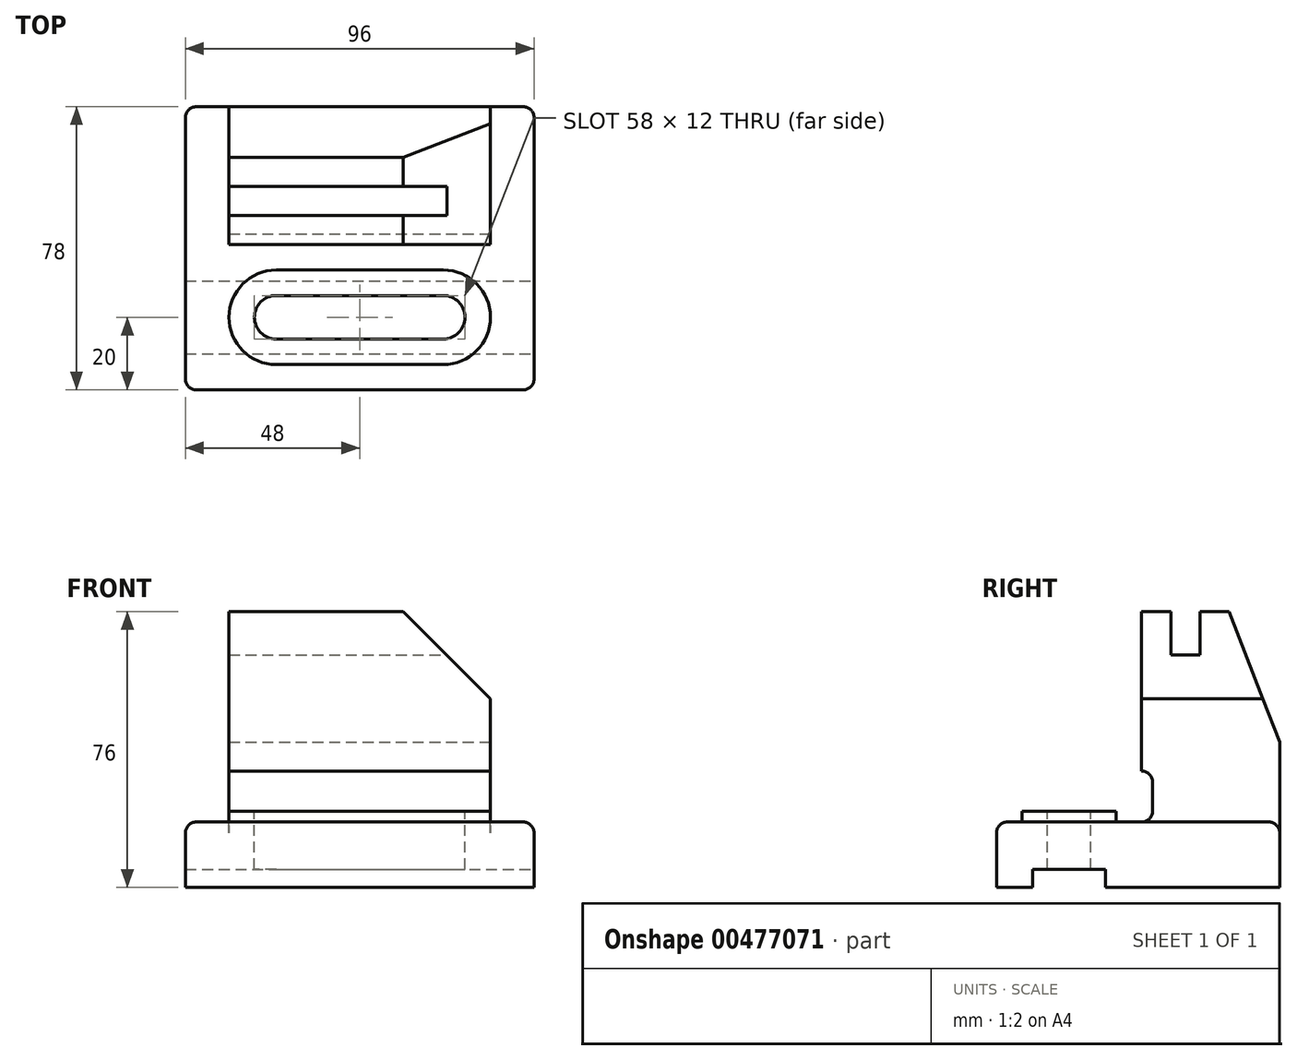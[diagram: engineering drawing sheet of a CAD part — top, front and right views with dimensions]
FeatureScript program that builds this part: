
annotation { "Feature Type Name" : "Feature", "Feature Type Description" : "" }
export const myFeature = defineFeature(function(context is Context, id is Id, definition is map)
    precondition{}
    {
        {
            var Q0;
            Q0=qCreatedBy(makeId("Top.planeOp"),FACE);
            var sketch = newSketch(context, id + "F0", { "sketchPlane" : qUnion([Q0])});
            skLineSegment(sketch, "E0.bottom", {"start": v(0, 0) * mm, "end": v(96, 0) * mm});
            skLineSegment(sketch, "E0.top", {"start": v(0, 78) * mm, "end": v(96, 78) * mm});
            skLineSegment(sketch, "E0.left", {"start": v(0, 0) * mm, "end": v(0, 78) * mm});
            skLineSegment(sketch, "E0.right", {"start": v(96, 0) * mm, "end": v(96, 78) * mm});
            skSolve(sketch);
        }
        {
            var Q0;
            Q0 = qSketchRegion(id + "F0", true);
            extrude(context, id + "F1", {"entities" : qUnion([Q0]), "depth" : 18 * mm});
        }
        {
            var Q0;
            Q0=makeQuery(id+"F1.opExtrude","CAP_FACE",FACE,{"disambiguationData":[OSD([sQuery(id+"F0.wireOp",EDGE,"E0.bottom"),sQuery(id+"F0.wireOp",EDGE,"E0.top"),sQuery(id+"F0.wireOp",EDGE,"E0.left"),sQuery(id+"F0.wireOp",EDGE,"E0.right")])],"isStart":false});
            var sketch = newSketch(context, id + "F2", { "sketchPlane" : qUnion([Q0])});
            skLineSegment(sketch, "E1.bottom", {"start": v(12, 78) * mm, "end": v(84, 78) * mm});
            skLineSegment(sketch, "E1.top", {"start": v(12, 40) * mm, "end": v(84, 40) * mm});
            skLineSegment(sketch, "E1.left", {"start": v(12, 78) * mm, "end": v(12, 40) * mm});
            skLineSegment(sketch, "E1.right", {"start": v(84, 78) * mm, "end": v(84, 40) * mm});
            skSolve(sketch);
        }
        {
            var Q0;
            Q0 = qSketchRegion(id + "F2", true);
            extrude(context, id + "F3", {"entities" : qUnion([Q0]), "operationType" : NewBodyOperationType.ADD, "depth" : 58 * mm});
        }
        {
            var Q0;
            {var subQ0=sQuery(id+"F0.wireOp",EDGE,"E0.right");var subQ1=sQuery(id+"F0.wireOp",EDGE,"E0.top");Q0=makeQuery(id+"F3.boolean.opBoolean","SPLIT",EDGE,{"disambiguationData":[TD([makeQuery(id+"F1.opExtrude","SWEPT_FACE",FACE,{"disambiguationData":[OSD([subQ0])]})])],"derivedFrom":makeQuery(id+"F1.opExtrude","CAP_EDGE",EDGE,{"disambiguationData":[OSD([subQ1])],"isStart":false})});}
            var Q1;
            {var subQ0=sQuery(id+"F0.wireOp",EDGE,"E0.left");var subQ1=sQuery(id+"F0.wireOp",EDGE,"E0.top");Q1=makeQuery(id+"F3.boolean.opBoolean","SPLIT",EDGE,{"disambiguationData":[TD([makeQuery(id+"F1.opExtrude","SWEPT_FACE",FACE,{"disambiguationData":[OSD([subQ0])]})])],"derivedFrom":makeQuery(id+"F1.opExtrude","CAP_EDGE",EDGE,{"disambiguationData":[OSD([subQ1])],"isStart":false})});}
            fillet(context, id + "F4", {"entities" : qUnion([Q0, Q1]), "radius" : 3 * mm, "allowEdgeOverflow" : false});
        }
        {
            var Q0;
            Q0=makeQuery(id+"F3.opExtrude","CAP_FACE",FACE,{"disambiguationData":[OSD([sQuery(id+"F2.wireOp",EDGE,"E1.bottom"),sQuery(id+"F2.wireOp",EDGE,"E1.top"),sQuery(id+"F2.wireOp",EDGE,"E1.left"),sQuery(id+"F2.wireOp",EDGE,"E1.right")])],"isStart":false});
            var sketch = newSketch(context, id + "F5", { "sketchPlane" : qUnion([Q0])});
            skLineSegment(sketch, "E2.bottom", {"start": v(12, 56) * mm, "end": v(84, 56) * mm});
            skLineSegment(sketch, "E2.top", {"start": v(12, 48) * mm, "end": v(84, 48) * mm});
            skLineSegment(sketch, "E2.left", {"start": v(12, 56) * mm, "end": v(12, 48) * mm});
            skLineSegment(sketch, "E2.right", {"start": v(84, 56) * mm, "end": v(84, 48) * mm});
            skSolve(sketch);
        }
        {
            var Q0;
            Q0 = qSketchRegion(id + "F5", true);
            extrude(context, id + "F6", {"entities" : qUnion([Q0]), "operationType" : NewBodyOperationType.REMOVE, "oppositeDirection" : true, "depth" : 12 * mm});
        }
        {
            var Q0;
            {var subQ0=sQuery(id+"F2.wireOp",EDGE,"E1.right");Q0=makeQuery(id+"F6.boolean.opBoolean","SPLIT",EDGE,{"disambiguationData":[TD([makeQuery(id+"F1.opExtrude","SWEPT_FACE",FACE,{"disambiguationData":[OSD([sQuery(id+"F0.wireOp",EDGE,"E0.top")])]})])],"derivedFrom":makeQuery(id+"F3.opExtrude","CAP_EDGE",EDGE,{"disambiguationData":[OSD([subQ0])],"isStart":false})});}
            var Q1;
            {var subQ0=sQuery(id+"F2.wireOp",EDGE,"E1.right");var subQ1=sQuery(id+"F2.wireOp",EDGE,"E1.top");Q1=makeQuery(id+"F6.boolean.opBoolean","SPLIT",EDGE,{"disambiguationData":[TD([makeQuery(id+"F3.opExtrude","SWEPT_FACE",FACE,{"disambiguationData":[OSD([subQ1])]})])],"derivedFrom":makeQuery(id+"F3.opExtrude","CAP_EDGE",EDGE,{"disambiguationData":[OSD([subQ0])],"isStart":false})});}
            chamfer(context, id + "F7", {"entities" : qUnion([Q0, Q1]), "width" : 24 * mm, "tangentPropagation" : true});
        }
        {
            var Q0;
            Q0=makeQuery(id+"F3.opExtrude","CAP_EDGE",EDGE,{"disambiguationData":[OSD([sQuery(id+"F2.wireOp",EDGE,"E1.bottom")])],"isStart":false});
            chamfer(context, id + "F8", {"entities" : qUnion([Q0]), "chamferType" : ChamferType.TWO_OFFSETS, "width1" : 36 * mm, "oppositeDirection" : false, "width2" : 14 * mm, "tangentPropagation" : true});
        }
        {
            var Q0;
            Q0=makeQuery(id+"F3.opExtrude","SWEPT_FACE",FACE,{"disambiguationData":[OSD([sQuery(id+"F2.wireOp",EDGE,"E1.right")])]});
            var sketch = newSketch(context, id + "F9", { "sketchPlane" : qUnion([Q0])});
            skLineSegment(sketch, "E3.bottom", {"start": v(40, 18) * mm, "end": v(43, 18) * mm});
            skLineSegment(sketch, "E3.top", {"start": v(40, 32) * mm, "end": v(43, 32) * mm});
            skLineSegment(sketch, "E3.left", {"start": v(40, 18) * mm, "end": v(40, 32) * mm});
            skLineSegment(sketch, "E3.right", {"start": v(43, 18) * mm, "end": v(43, 32) * mm});
            skSolve(sketch);
        }
        {
            var Q0;
            Q0 = qSketchRegion(id + "F9", true);
            extrude(context, id + "F10", {"entities" : qUnion([Q0]), "operationType" : NewBodyOperationType.REMOVE, "endBound" : BoundingType.UP_TO_NEXT, "oppositeDirection" : true, "depth" : 25 * mm});
        }
        {
            var Q0;
            Q0=makeQuery(id+"F1.opExtrude","SWEPT_FACE",FACE,{"disambiguationData":[OSD([sQuery(id+"F0.wireOp",EDGE,"E0.right")])]});
            var sketch = newSketch(context, id + "F11", { "sketchPlane" : qUnion([Q0])});
            skLineSegment(sketch, "E4.bottom", {"start": v(10, 0) * mm, "end": v(30, 0) * mm});
            skLineSegment(sketch, "E4.top", {"start": v(10, 5) * mm, "end": v(30, 5) * mm});
            skLineSegment(sketch, "E4.left", {"start": v(10, 0) * mm, "end": v(10, 5) * mm});
            skLineSegment(sketch, "E4.right", {"start": v(30, 0) * mm, "end": v(30, 5) * mm});
            skSolve(sketch);
        }
        {
            var Q0;
            Q0 = qSketchRegion(id + "F11", true);
            extrude(context, id + "F12", {"entities" : qUnion([Q0]), "operationType" : NewBodyOperationType.REMOVE, "endBound" : BoundingType.UP_TO_NEXT, "oppositeDirection" : true, "depth" : 25 * mm});
        }
        {
            var Q0;
            Q0=makeQuery(id+"F10.boolean.opBoolean","MERGE",FACE,{"derivedFrom":[makeQuery(id+"F1.opExtrude","CAP_FACE",FACE,{"disambiguationData":[OSD([sQuery(id+"F0.wireOp",EDGE,"E0.bottom"),sQuery(id+"F0.wireOp",EDGE,"E0.top"),sQuery(id+"F0.wireOp",EDGE,"E0.left"),sQuery(id+"F0.wireOp",EDGE,"E0.right")])],"isStart":false}),makeQuery(id+"F10.opExtrude","SWEPT_FACE",FACE,{"disambiguationData":[OSD([sQuery(id+"F9.wireOp",EDGE,"E3.bottom")])]})]});
            var sketch = newSketch(context, id + "F13", { "sketchPlane" : qUnion([Q0])});
            skLineSegment(sketch, "E5", {"start": v(25, 20) * mm, "end": v(71, 20) * mm, "construction": true});
            skLineSegment(sketch, "E6", {"start": v(71, 33) * mm, "end": v(25, 33) * mm});
            skLineSegment(sketch, "E7.MirrorCS", {"start": v(71, 7) * mm, "end": v(25, 7) * mm});
            skArc(sketch, "E8", {"start": v(25, 7) * mm, "mid": v(12, 20) * mm, "end": v(25, 33) * mm});
            skArc(sketch, "E9", {"start": v(71, 33) * mm, "mid": v(84, 20) * mm, "end": v(71, 7) * mm});
            skSolve(sketch);
        }
        {
            var Q0;
            Q0 = qSketchRegion(id + "F13", true);
            extrude(context, id + "F14", {"entities" : qUnion([Q0]), "operationType" : NewBodyOperationType.ADD, "depth" : 3 * mm});
        }
        {
            var Q0;
            Q0=makeQuery(id+"F14.opExtrude","CAP_FACE",FACE,{"disambiguationData":[OSD([sQuery(id+"F13.wireOp",EDGE,"E6"),sQuery(id+"F13.wireOp",EDGE,"E7.MirrorCS"),sQuery(id+"F13.wireOp",EDGE,"E8"),sQuery(id+"F13.wireOp",EDGE,"E9")])],"isStart":false});
            var sketch = newSketch(context, id + "F15", { "sketchPlane" : qUnion([Q0])});
            skLineSegment(sketch, "E10.JbB.JbB", {"start": v(25, 20) * mm, "end": v(71, 20) * mm, "construction": true});
            skArc(sketch, "E10.0.startCap", {"start": v(25, 14) * mm, "mid": v(19, 20) * mm, "end": v(25, 26) * mm});
            skArc(sketch, "E10.0.endCap", {"start": v(71, 26) * mm, "mid": v(77, 20) * mm, "end": v(71, 14) * mm});
            skLineSegment(sketch, "E10.0.left", {"start": v(25, 26) * mm, "end": v(71, 26) * mm});
            skLineSegment(sketch, "E10.0.right", {"start": v(25, 14) * mm, "end": v(71, 14) * mm});
            skSolve(sketch);
        }
        {
            var Q0;
            Q0 = qSketchRegion(id + "F15", true);
            extrude(context, id + "F16", {"entities" : qUnion([Q0]), "operationType" : NewBodyOperationType.REMOVE, "endBound" : BoundingType.UP_TO_NEXT, "oppositeDirection" : true, "depth" : 25 * mm});
        }
        {
            var Q0;
            Q0=makeQuery(id+"F1.opExtrude","SWEPT_EDGE",EDGE,{"disambiguationData":[OSD([sQuery(id+"F0.wireOp",EDGE,"E0.bottom"),sQuery(id+"F0.wireOp",EDGE,"E0.left")])]});
            var Q1;
            Q1=makeQuery(id+"F1.opExtrude","CAP_EDGE",EDGE,{"disambiguationData":[OSD([sQuery(id+"F0.wireOp",EDGE,"E0.bottom")])],"isStart":false});
            var Q2;
            Q2=makeQuery(id+"F1.opExtrude","CAP_EDGE",EDGE,{"disambiguationData":[OSD([sQuery(id+"F0.wireOp",EDGE,"E0.left")])],"isStart":false});
            var Q3;
            Q3=makeQuery(id+"F1.opExtrude","SWEPT_EDGE",EDGE,{"disambiguationData":[OSD([sQuery(id+"F0.wireOp",EDGE,"E0.bottom"),sQuery(id+"F0.wireOp",EDGE,"E0.right")])]});
            var Q4;
            Q4=makeQuery(id+"F1.opExtrude","SWEPT_EDGE",EDGE,{"disambiguationData":[OSD([sQuery(id+"F0.wireOp",EDGE,"E0.top"),sQuery(id+"F0.wireOp",EDGE,"E0.left")])]});
            var Q5;
            Q5=makeQuery(id+"F10.boolean.opBoolean","COPY",EDGE,{"derivedFrom":makeQuery(id+"F10.opExtrude","SWEPT_EDGE",EDGE,{"disambiguationData":[OSD([sQuery(id+"F9.wireOp",EDGE,"E3.top"),sQuery(id+"F9.wireOp",EDGE,"E3.right")])]})});
            var Q6;
            Q6=makeQuery(id+"F10.boolean.opBoolean","COPY",EDGE,{"derivedFrom":makeQuery(id+"F10.opExtrude","SWEPT_EDGE",EDGE,{"disambiguationData":[OSD([sQuery(id+"F2.wireOp",EDGE,"E1.right"),sQuery(id+"F9.wireOp",EDGE,"E3.bottom"),sQuery(id+"F9.wireOp",EDGE,"E3.right")])]})});
            var Q7;
            Q7=makeQuery(id+"F1.opExtrude","CAP_EDGE",EDGE,{"disambiguationData":[OSD([sQuery(id+"F0.wireOp",EDGE,"E0.right")])],"isStart":false});
            var Q8;
            Q8=makeQuery(id+"F1.opExtrude","SWEPT_EDGE",EDGE,{"disambiguationData":[OSD([sQuery(id+"F0.wireOp",EDGE,"E0.top"),sQuery(id+"F0.wireOp",EDGE,"E0.right")])]});
            var Q9;
            Q9=makeQuery(id+"F3.opExtrude","CAP_EDGE",EDGE,{"disambiguationData":[OSD([sQuery(id+"F2.wireOp",EDGE,"E1.right")])],"isStart":true});
            var Q10;
            Q10=makeQuery(id+"F3.opExtrude","CAP_EDGE",EDGE,{"disambiguationData":[OSD([sQuery(id+"F2.wireOp",EDGE,"E1.left")])],"isStart":true});
            var Q11;
            Q11=makeQuery(id+"F14.opExtrude","CAP_EDGE",EDGE,{"disambiguationData":[OSD([sQuery(id+"F13.wireOp",EDGE,"E8")])],"isStart":true});
            fillet(context, id + "F17", {"entities" : qUnion([Q0, Q1, Q2, Q3, Q4, Q5, Q6, Q7, Q8, Q9, Q10, Q11]), "radius" : 3 * mm, "tangentPropagation" : true, "allowEdgeOverflow" : false});
        }
    });
